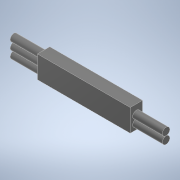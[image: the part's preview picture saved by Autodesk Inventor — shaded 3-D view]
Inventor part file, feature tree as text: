
AUTODESK INVENTOR PART (.ipt)
format: ipt  version: 2022 (Build 260153000, 153)  size: 120,832 bytes
history: native  units: in
note: dims shown in document units (in); Inventor stores cm internally (conversion verified against a paired STEP export)
features: extrude x3, sketch x2
ambient origin geometry x8: Origin, YZ Plane, XZ Plane, XY Plane, X Axis, Y Axis, Z Axis, Center Point
bodies: Solid1 (feature_tree)
feature tree (5):
  extrude  "Extrusion1"  Depth=0.3543in
  extrude  "Extrusion2"  Depth=0.4724in
  extrude  "Extrusion3"  Depth=0.4724in TaperAngle=0.0deg
  sketch  "Sketch1"  dims[d0=1.4764in d1=0.3543in]
  sketch  "Sketch3"  dims[d2=0.1969in d3=0.0in d4=0.1181in d7=0.4724in d8=0.0in d11=0.1181in d12=0.4724in d13=0.0in]
